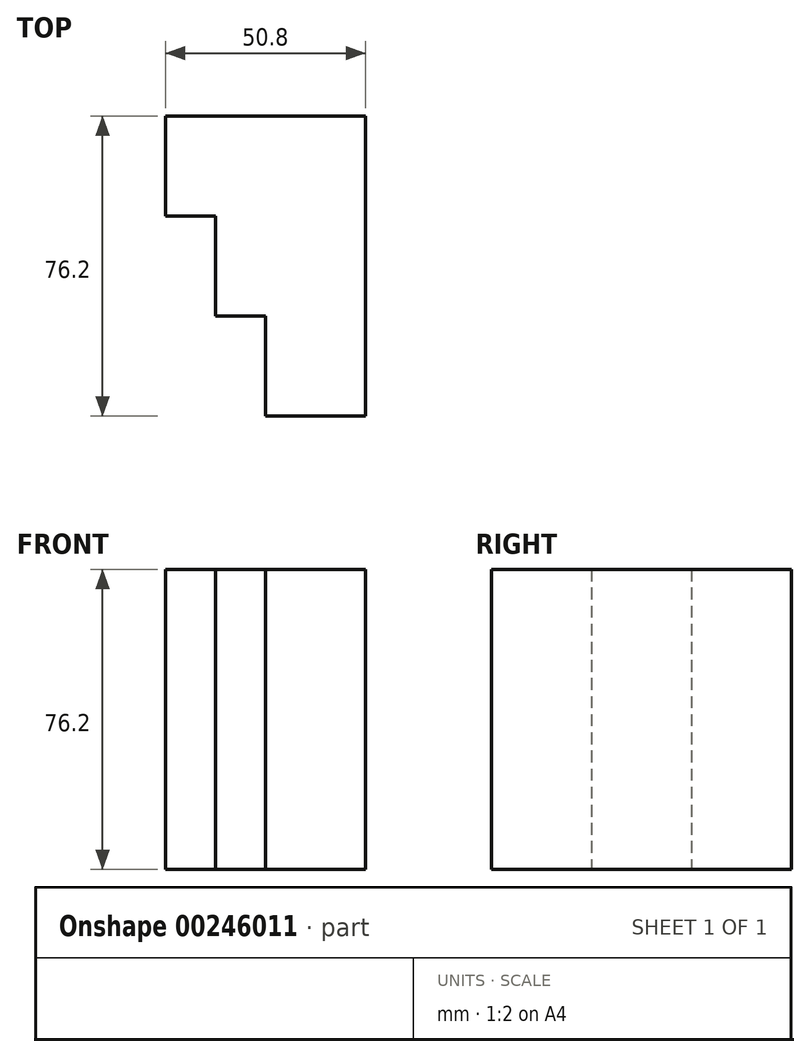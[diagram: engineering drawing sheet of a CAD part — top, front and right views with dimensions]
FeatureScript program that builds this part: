
annotation { "Feature Type Name" : "Feature", "Feature Type Description" : "" }
export const myFeature = defineFeature(function(context is Context, id is Id, definition is map)
    precondition{}
    {
        {
            var Q0;
            Q0=qCreatedBy(makeId("Top.planeOp"),FACE);
            var sketch = newSketch(context, id + "F0", { "sketchPlane" : qUnion([Q0])});
            skLineSegment(sketch, "E0", {"start": v(-13.2, -58.49) * mm, "end": v(12.2, -58.49) * mm});
            skLineSegment(sketch, "E1", {"start": v(12.2, -58.49) * mm, "end": v(12.2, 17.71) * mm});
            skLineSegment(sketch, "E2", {"start": v(12.2, 17.71) * mm, "end": v(-38.6, 17.71) * mm});
            skLineSegment(sketch, "E3", {"start": v(-38.6, 17.71) * mm, "end": v(-38.6, -7.69) * mm});
            skLineSegment(sketch, "E4", {"start": v(-38.6, -7.69) * mm, "end": v(-25.9, -7.69) * mm});
            skLineSegment(sketch, "E5", {"start": v(-25.9, -7.69) * mm, "end": v(-25.9, -33.09) * mm});
            skLineSegment(sketch, "E6", {"start": v(-25.9, -33.09) * mm, "end": v(-13.2, -33.09) * mm});
            skLineSegment(sketch, "E7", {"start": v(-13.2, -33.09) * mm, "end": v(-13.2, -58.49) * mm});
            skSolve(sketch);
        }
        {
            var Q0;
            Q0 = qSketchRegion(id + "F0", true);
            extrude(context, id + "F1", {"entities" : qUnion([Q0]), "depth" : 76.2 * mm});
        }
    });
